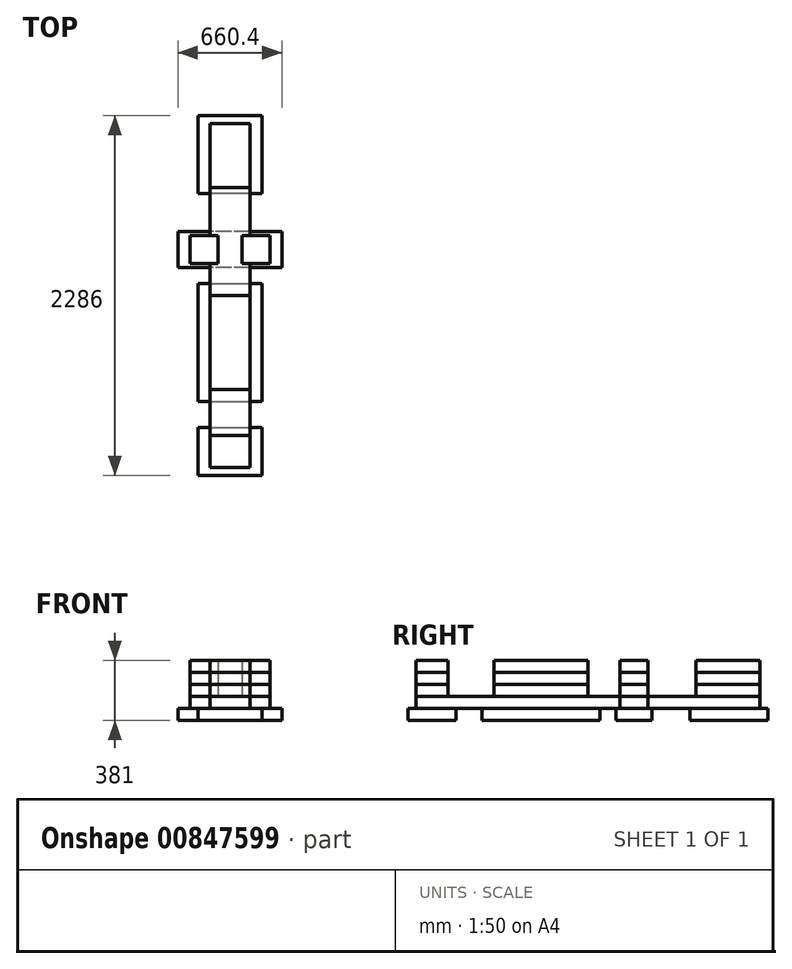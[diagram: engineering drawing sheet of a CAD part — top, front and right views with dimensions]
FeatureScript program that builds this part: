
annotation { "Feature Type Name" : "Feature", "Feature Type Description" : "" }
export const myFeature = defineFeature(function(context is Context, id is Id, definition is map)
    precondition{}
    {
        {
            var Q0;
            Q0=qCreatedBy(makeId("Top.planeOp"),FACE);
            var sketch = newSketch(context, id + "F0", { "sketchPlane" : qUnion([Q0])});
            skLineSegment(sketch, "E0.bottom", {"start": v(-251.07, -477.1) * mm, "end": v(155.33, -477.1) * mm});
            skLineSegment(sketch, "E0.top", {"start": v(-251.07, -781.9) * mm, "end": v(155.33, -781.9) * mm});
            skLineSegment(sketch, "E0.left", {"start": v(-251.07, -477.1) * mm, "end": v(-251.07, -781.9) * mm});
            skLineSegment(sketch, "E0.right", {"start": v(155.33, -477.1) * mm, "end": v(155.33, -781.9) * mm});
            skLineSegment(sketch, "E1.bottom", {"start": v(-251.07, -312) * mm, "end": v(155.33, -312) * mm});
            skLineSegment(sketch, "E1.top", {"start": v(-251.07, 437.3) * mm, "end": v(155.33, 437.3) * mm});
            skLineSegment(sketch, "E1.left", {"start": v(-251.07, -312) * mm, "end": v(-251.07, 437.3) * mm});
            skLineSegment(sketch, "E1.right", {"start": v(155.33, -312) * mm, "end": v(155.33, 437.3) * mm});
            skLineSegment(sketch, "E2.bottom", {"start": v(282.33, 538.9) * mm, "end": v(-378.07, 538.9) * mm});
            skLineSegment(sketch, "E2.top", {"start": v(282.33, 767.5) * mm, "end": v(-378.07, 767.5) * mm});
            skLineSegment(sketch, "E2.left", {"start": v(282.33, 538.9) * mm, "end": v(282.33, 767.5) * mm});
            skLineSegment(sketch, "E2.right", {"start": v(-378.07, 538.9) * mm, "end": v(-378.07, 767.5) * mm});
            skLineSegment(sketch, "E3.bottom", {"start": v(155.33, 1008.8) * mm, "end": v(-251.07, 1008.8) * mm});
            skLineSegment(sketch, "E3.top", {"start": v(155.33, 1504.1) * mm, "end": v(-251.07, 1504.1) * mm});
            skLineSegment(sketch, "E3.left", {"start": v(155.33, 1008.8) * mm, "end": v(155.33, 1504.1) * mm});
            skLineSegment(sketch, "E3.right", {"start": v(-251.07, 1008.8) * mm, "end": v(-251.07, 1504.1) * mm});
            skLineSegment(sketch, "E4", {"start": v(-47.87, -781.9) * mm, "end": v(-47.87, 1504.1) * mm, "construction": true});
            skSolve(sketch);
        }
        {
            var Q0;
            Q0=makeQuery(id+"F0.imprint","IMPRINT",FACE,{"disambiguationData":[TD([[makeQuery(id+"F0.imprint","IMPRINT",EDGE,{"derivedFrom":sQuery(id+"F0.wireOp",EDGE,"E0.bottom")}),-1.0]])]});
            var Q1;
            Q1=makeQuery(id+"F0.imprint","IMPRINT",FACE,{"disambiguationData":[TD([[makeQuery(id+"F0.imprint","IMPRINT",EDGE,{"derivedFrom":sQuery(id+"F0.wireOp",EDGE,"E1.bottom")}),1.0]])]});
            var Q2;
            Q2=makeQuery(id+"F0.imprint","IMPRINT",FACE,{"disambiguationData":[TD([[makeQuery(id+"F0.imprint","IMPRINT",EDGE,{"derivedFrom":sQuery(id+"F0.wireOp",EDGE,"E2.bottom")}),-1.0]])]});
            var Q3;
            Q3=makeQuery(id+"F0.imprint","IMPRINT",FACE,{"disambiguationData":[TD([[makeQuery(id+"F0.imprint","IMPRINT",EDGE,{"derivedFrom":sQuery(id+"F0.wireOp",EDGE,"E3.bottom")}),-1.0]])]});
            extrude(context, id + "F1", {"entities" : qUnion([Q0, Q1, Q2, Q3]), "depth" : 76.2 * mm, "offsetDistance" : 25.4 * mm});
        }
        {
            var Q0;
            Q0=makeQuery(id+"F1.opExtrude","CAP_FACE",FACE,{"disambiguationData":[OSD([sQuery(id+"F0.wireOp",EDGE,"E0.bottom"),sQuery(id+"F0.wireOp",EDGE,"E0.top"),sQuery(id+"F0.wireOp",EDGE,"E0.left"),sQuery(id+"F0.wireOp",EDGE,"E0.right")])],"isStart":false});
            var sketch = newSketch(context, id + "F2", { "sketchPlane" : qUnion([Q0])});
            skLineSegment(sketch, "E5", {"start": v(-174.87, -731.1) * mm, "end": v(-174.87, 564.3) * mm});
            skLineSegment(sketch, "E6", {"start": v(-174.87, 564.3) * mm, "end": v(-301.87, 564.3) * mm});
            skLineSegment(sketch, "E7", {"start": v(-301.87, 564.3) * mm, "end": v(-301.87, 742.1) * mm});
            skLineSegment(sketch, "E8", {"start": v(-301.87, 742.1) * mm, "end": v(-174.87, 742.1) * mm});
            skLineSegment(sketch, "E9", {"start": v(-174.87, 742.1) * mm, "end": v(-174.87, 1453.3) * mm});
            skLineSegment(sketch, "E10", {"start": v(-174.87, 1453.3) * mm, "end": v(79.13, 1453.3) * mm});
            skLineSegment(sketch, "E11", {"start": v(79.13, 1453.3) * mm, "end": v(79.13, 742.1) * mm});
            skLineSegment(sketch, "E12", {"start": v(79.13, 742.1) * mm, "end": v(206.13, 742.1) * mm});
            skLineSegment(sketch, "E13", {"start": v(206.13, 742.1) * mm, "end": v(206.13, 564.3) * mm});
            skLineSegment(sketch, "E14", {"start": v(206.13, 564.3) * mm, "end": v(79.13, 564.3) * mm});
            skLineSegment(sketch, "E15", {"start": v(79.13, 564.3) * mm, "end": v(79.13, -731.1) * mm});
            skLineSegment(sketch, "E16", {"start": v(79.13, -731.1) * mm, "end": v(-174.87, -731.1) * mm});
            skSolve(sketch);
        }
        {
            var Q0;
            {var subQ1=sQuery(id+"F2.wireOp",EDGE,"E6");Q0=makeQuery(id+"F2.imprint","IMPRINT",FACE,{"disambiguationData":[TD([[makeQuery(id+"F2.imprint","IMPRINT",EDGE,{"derivedFrom":subQ1}),-1.0]])]});}
            var Q1;
            {var subQ0=sQuery(id+"F2.wireOp",EDGE,"E16");Q1=makeQuery(id+"F2.imprint","IMPRINT",FACE,{"disambiguationData":[TD([[makeQuery(id+"F2.imprint","IMPRINT",EDGE,{"derivedFrom":subQ0}),-1.0]])]});}
            extrude(context, id + "F3", {"entities" : qUnion([Q0, Q1]), "depth" : 76.2 * mm, "offsetDistance" : 25.4 * mm});
        }
        {
            var Q0;
            Q0=makeQuery(id+"F3.opExtrude","CAP_FACE",FACE,{"disambiguationData":[OSD([sQuery(id+"F2.wireOp",EDGE,"E5"),sQuery(id+"F2.wireOp",EDGE,"E6"),sQuery(id+"F2.wireOp",EDGE,"E7"),sQuery(id+"F2.wireOp",EDGE,"E8"),sQuery(id+"F2.wireOp",EDGE,"E9"),sQuery(id+"F2.wireOp",EDGE,"E10"),sQuery(id+"F2.wireOp",EDGE,"E11"),sQuery(id+"F2.wireOp",EDGE,"E12"),sQuery(id+"F2.wireOp",EDGE,"E13"),sQuery(id+"F2.wireOp",EDGE,"E14"),sQuery(id+"F2.wireOp",EDGE,"E15"),sQuery(id+"F2.wireOp",EDGE,"E16")])],"isStart":false});
            var sketch = newSketch(context, id + "F4", { "sketchPlane" : qUnion([Q0])});
            skLineSegment(sketch, "E17", {"start": v(-174.87, -731.1) * mm, "end": v(-174.87, -527.9) * mm});
            skLineSegment(sketch, "E18", {"start": v(-174.87, -527.9) * mm, "end": v(79.13, -527.9) * mm});
            skLineSegment(sketch, "E19", {"start": v(79.13, -527.9) * mm, "end": v(79.13, -731.1) * mm});
            skLineSegment(sketch, "E20", {"start": v(79.13, -731.1) * mm, "end": v(-174.87, -731.1) * mm});
            skLineSegment(sketch, "E21", {"start": v(-174.87, -235.8) * mm, "end": v(-174.87, 361.1) * mm});
            skLineSegment(sketch, "E22", {"start": v(-174.87, 361.1) * mm, "end": v(79.13, 361.1) * mm});
            skLineSegment(sketch, "E23", {"start": v(79.13, 361.1) * mm, "end": v(79.13, -235.8) * mm});
            skLineSegment(sketch, "E24", {"start": v(79.13, -235.8) * mm, "end": v(-174.87, -235.8) * mm});
            skLineSegment(sketch, "E25", {"start": v(-301.87, 564.3) * mm, "end": v(-301.87, 742.1) * mm});
            skLineSegment(sketch, "E26", {"start": v(-301.87, 742.1) * mm, "end": v(-124.07, 742.1) * mm});
            skLineSegment(sketch, "E27", {"start": v(-124.07, 742.1) * mm, "end": v(-124.07, 564.3) * mm});
            skLineSegment(sketch, "E28", {"start": v(-124.07, 564.3) * mm, "end": v(-301.87, 564.3) * mm});
            skLineSegment(sketch, "E29", {"start": v(28.33, 742.1) * mm, "end": v(206.13, 742.1) * mm});
            skLineSegment(sketch, "E30", {"start": v(206.13, 742.1) * mm, "end": v(206.13, 564.3) * mm});
            skLineSegment(sketch, "E31", {"start": v(206.13, 564.3) * mm, "end": v(28.33, 564.3) * mm});
            skLineSegment(sketch, "E32", {"start": v(28.33, 564.3) * mm, "end": v(28.33, 742.1) * mm});
            skLineSegment(sketch, "E33", {"start": v(-174.87, 1046.9) * mm, "end": v(-174.87, 1453.3) * mm});
            skLineSegment(sketch, "E34", {"start": v(-174.87, 1453.3) * mm, "end": v(79.13, 1453.3) * mm});
            skLineSegment(sketch, "E35", {"start": v(79.13, 1453.3) * mm, "end": v(79.13, 1046.9) * mm});
            skLineSegment(sketch, "E36", {"start": v(79.13, 1046.9) * mm, "end": v(-174.87, 1046.9) * mm});
            skSolve(sketch);
        }
        {
            var Q0;
            Q0=makeQuery(id+"F4.imprint","IMPRINT",FACE,{"disambiguationData":[TD([[makeQuery(id+"F4.imprint","IMPRINT",EDGE,{"derivedFrom":sQuery(id+"F4.wireOp",EDGE,"E17")}),-1.0]])]});
            var Q1;
            Q1=makeQuery(id+"F4.imprint","IMPRINT",FACE,{"disambiguationData":[TD([[makeQuery(id+"F4.imprint","IMPRINT",EDGE,{"derivedFrom":sQuery(id+"F4.wireOp",EDGE,"E21")}),-1.0]])]});
            var Q2;
            {var subQ3=sQuery(id+"F4.wireOp",EDGE,"E25");Q2=makeQuery(id+"F4.imprint","IMPRINT",FACE,{"disambiguationData":[TD([[makeQuery(id+"F4.imprint","IMPRINT",EDGE,{"derivedFrom":subQ3}),-1.0]])]});}
            var Q3;
            {var subQ1=sQuery(id+"F4.wireOp",EDGE,"E30");Q3=makeQuery(id+"F4.imprint","IMPRINT",FACE,{"disambiguationData":[TD([[makeQuery(id+"F4.imprint","IMPRINT",EDGE,{"derivedFrom":subQ1}),-1.0]])]});}
            var Q4;
            Q4=makeQuery(id+"F4.imprint","IMPRINT",FACE,{"disambiguationData":[TD([[makeQuery(id+"F4.imprint","IMPRINT",EDGE,{"derivedFrom":sQuery(id+"F4.wireOp",EDGE,"E33")}),-1.0]])]});
            extrude(context, id + "F5", {"entities" : qUnion([Q0, Q1, Q2, Q3, Q4]), "depth" : 76.2 * mm, "offsetDistance" : 25.4 * mm});
        }
        {
            var Q0;
            Q0=makeQuery(id+"F5.opExtrude","CAP_FACE",FACE,{"disambiguationData":[OSD([sQuery(id+"F4.wireOp",EDGE,"E17"),sQuery(id+"F4.wireOp",EDGE,"E18"),sQuery(id+"F4.wireOp",EDGE,"E19"),sQuery(id+"F4.wireOp",EDGE,"E20")])],"isStart":false});
            var Q1;
            Q1=makeQuery(id+"F5.opExtrude","CAP_FACE",FACE,{"disambiguationData":[OSD([sQuery(id+"F4.wireOp",EDGE,"E21"),sQuery(id+"F4.wireOp",EDGE,"E22"),sQuery(id+"F4.wireOp",EDGE,"E23"),sQuery(id+"F4.wireOp",EDGE,"E24")])],"isStart":false});
            var Q2;
            Q2=makeQuery(id+"F5.opExtrude","CAP_FACE",FACE,{"disambiguationData":[OSD([sQuery(id+"F4.wireOp",EDGE,"E25"),sQuery(id+"F4.wireOp",EDGE,"E26"),sQuery(id+"F4.wireOp",EDGE,"E27"),sQuery(id+"F4.wireOp",EDGE,"E28")])],"isStart":false});
            var Q3;
            Q3=makeQuery(id+"F5.opExtrude","CAP_FACE",FACE,{"disambiguationData":[OSD([sQuery(id+"F4.wireOp",EDGE,"E29"),sQuery(id+"F4.wireOp",EDGE,"E30"),sQuery(id+"F4.wireOp",EDGE,"E31"),sQuery(id+"F4.wireOp",EDGE,"E32")])],"isStart":false});
            var Q4;
            Q4=makeQuery(id+"F5.opExtrude","CAP_FACE",FACE,{"disambiguationData":[OSD([sQuery(id+"F4.wireOp",EDGE,"E33"),sQuery(id+"F4.wireOp",EDGE,"E34"),sQuery(id+"F4.wireOp",EDGE,"E35"),sQuery(id+"F4.wireOp",EDGE,"E36")])],"isStart":false});
            extrude(context, id + "F6", {"entities" : qUnion([Q0, Q1, Q2, Q3, Q4]), "depth" : 76.2 * mm, "offsetDistance" : 25.4 * mm});
        }
        {
            var Q0;
            Q0=makeQuery(id+"F6.opExtrude","CAP_FACE",FACE,{"disambiguationData":[OSD([sQuery(id+"F4.wireOp",EDGE,"E17"),sQuery(id+"F4.wireOp",EDGE,"E18"),sQuery(id+"F4.wireOp",EDGE,"E19"),sQuery(id+"F4.wireOp",EDGE,"E20")])],"isStart":false});
            var Q1;
            Q1=makeQuery(id+"F6.opExtrude","CAP_FACE",FACE,{"disambiguationData":[OSD([sQuery(id+"F4.wireOp",EDGE,"E21"),sQuery(id+"F4.wireOp",EDGE,"E22"),sQuery(id+"F4.wireOp",EDGE,"E23"),sQuery(id+"F4.wireOp",EDGE,"E24")])],"isStart":false});
            var Q2;
            Q2=makeQuery(id+"F6.opExtrude","CAP_FACE",FACE,{"disambiguationData":[OSD([sQuery(id+"F4.wireOp",EDGE,"E25"),sQuery(id+"F4.wireOp",EDGE,"E26"),sQuery(id+"F4.wireOp",EDGE,"E27"),sQuery(id+"F4.wireOp",EDGE,"E28")])],"isStart":false});
            var Q3;
            Q3=makeQuery(id+"F6.opExtrude","CAP_FACE",FACE,{"disambiguationData":[OSD([sQuery(id+"F4.wireOp",EDGE,"E29"),sQuery(id+"F4.wireOp",EDGE,"E30"),sQuery(id+"F4.wireOp",EDGE,"E31"),sQuery(id+"F4.wireOp",EDGE,"E32")])],"isStart":false});
            var Q4;
            Q4=makeQuery(id+"F6.opExtrude","CAP_FACE",FACE,{"disambiguationData":[OSD([sQuery(id+"F4.wireOp",EDGE,"E33"),sQuery(id+"F4.wireOp",EDGE,"E34"),sQuery(id+"F4.wireOp",EDGE,"E35"),sQuery(id+"F4.wireOp",EDGE,"E36")])],"isStart":false});
            extrude(context, id + "F7", {"entities" : qUnion([Q0, Q1, Q2, Q3, Q4]), "depth" : 76.2 * mm, "offsetDistance" : 25.4 * mm});
        }
    });
